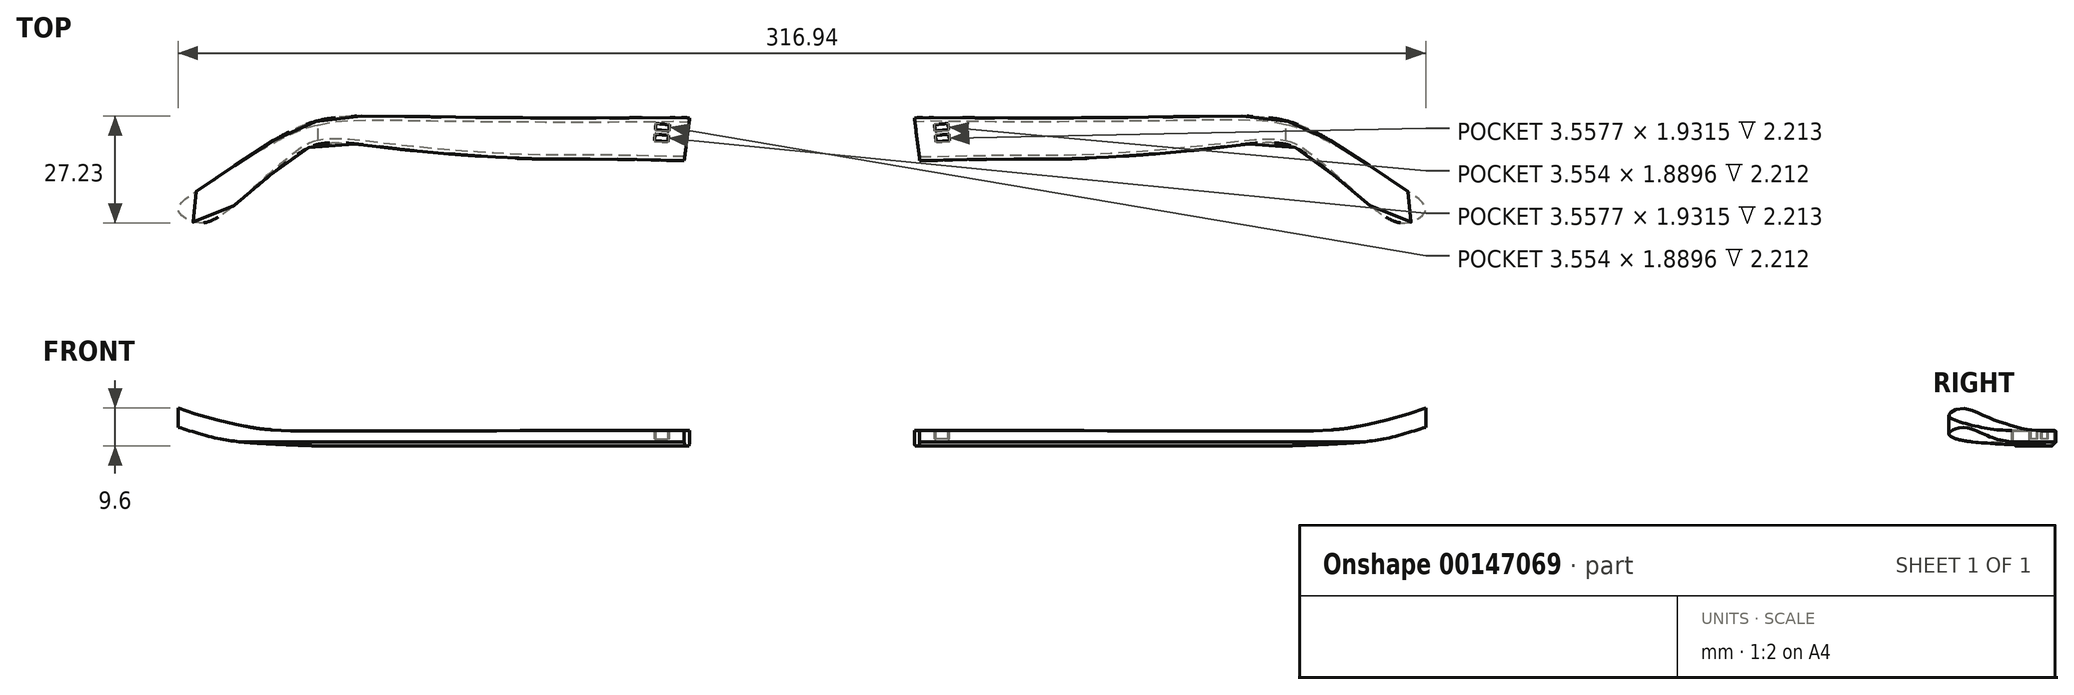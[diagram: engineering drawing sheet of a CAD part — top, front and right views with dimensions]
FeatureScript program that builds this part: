
annotation { "Feature Type Name" : "Feature", "Feature Type Description" : "" }
export const myFeature = defineFeature(function(context is Context, id is Id, definition is map)
    precondition{}
    {
        {
            var Q0;
            Q0=qCreatedBy(makeId("Top.planeOp"),FACE);
            var sketch = newSketch(context, id + "F0", { "sketchPlane" : qUnion([Q0])});
            skFitSpline(sketch, "E0", {"points": [v(-149.74, 2.86) * mm, v(-143.4, 7.26) * mm, v(-129.74, 15.62) * mm, v(-118.6, 18.94) * mm, v(-100.32, 19.28) * mm, v(-73.4, 18.94) * mm, v(-42.28, 18.93) * mm, v(-31.93, 19.03) * mm, v(-29.5, 18.93) * mm, v(-28, 18.65) * mm, v(-25.83, 16.47) * mm, v(-25.2, 12.13) * mm, v(-28.1, 8.49) * mm, v(-29.97, 8.11) * mm, v(-34.44, 8.11) * mm, v(-42.49, 8.3) * mm, v(-61.43, 8.47) * mm, v(-72.57, 8.64) * mm, v(-100.82, 10.8) * mm, v(-115.45, 12.46) * mm, v(-121.1, 12.46) * mm, v(-124.75, 11.63) * mm, v(-129.57, 8.64) * mm, v(-139.71, 0.5) * mm, v(-145.78, -4.53) * mm, v(-151.34, -7.65) * mm, v(-155.73, -7.18) * mm, v(-158.45, -4.45) * mm, v(-156.34, -1.45) * mm, v(-149.74, 2.86) * mm]});
            skSolve(sketch);
        }
        {
            var Q0;
            Q0=makeQuery(id+"F0.imprint","IMPRINT",FACE,{"disambiguationData":[TD([[makeQuery(id+"F0.imprint","IMPRINT",EDGE,{"derivedFrom":sQuery(id+"F0.wireOp",EDGE,"E0")}),-1.0]])]});
            extrude(context, id + "F1", {"entities" : qUnion([Q0]), "depth" : 10 * mm});
        }
        {
            var Q0;
            Q0=qCreatedBy(makeId("Front.planeOp"),FACE);
            var sketch = newSketch(context, id + "F2", { "sketchPlane" : qUnion([Q0])});
            skFitSpline(sketch, "E1", {"points": [v(-27.02, 3.92) * mm, v(-128.04, 3.8) * mm, v(-133.02, 4.02) * mm, v(-138.85, 4.55) * mm, v(-160.68, 10.48) * mm, v(-165.34, 12.18) * mm, v(-167.35, 10.06) * mm, v(-163.96, 6.88) * mm, v(-155.8, 3.92) * mm, v(-147.33, 1.7) * mm, v(-122.96, 0) * mm, v(-19.65, 0) * mm, v(-10.75, 2.75) * mm, v(-13.72, 3.39) * mm, v(-27.02, 3.92) * mm]});
            skSolve(sketch);
        }
        {
            var Q0;
            Q0=makeQuery(id+"F2.imprint","IMPRINT",FACE,{"disambiguationData":[TD([[makeQuery(id+"F2.imprint","IMPRINT",EDGE,{"derivedFrom":sQuery(id+"F2.wireOp",EDGE,"E1")}),1.0]])]});
            extrude(context, id + "F3", {"entities" : qUnion([Q0]), "operationType" : NewBodyOperationType.INTERSECT, "endBound" : BoundingType.SYMMETRIC, "depth" : 60 * mm});
        }
        {
            var Q0;
            Q0=qCreatedBy(makeId("Top.planeOp"),FACE);
            var sketch = newSketch(context, id + "F4", { "sketchPlane" : qUnion([Q0])});
            skLineSegment(sketch, "E2.bottom", {"start": v(-27.52, 26.98) * mm, "end": v(-9.8, 26.98) * mm});
            skLineSegment(sketch, "E2.top", {"start": v(-30.67, 2.24) * mm, "end": v(-9.8, 2.24) * mm});
            skLineSegment(sketch, "E2.left", {"start": v(-27.52, 26.98) * mm, "end": v(-30.67, 2.24) * mm});
            skLineSegment(sketch, "E2.right", {"start": v(-9.8, 26.98) * mm, "end": v(-9.8, 2.24) * mm});
            skSolve(sketch);
        }
        {
            var Q0;
            Q0 = qSketchRegion(id + "F4", true);
            extrude(context, id + "F5", {"entities" : qUnion([Q0]), "operationType" : NewBodyOperationType.REMOVE, "depth" : 25.4 * mm});
        }
        {
            var Q0;
            Q0=qCreatedBy(makeId("Top.planeOp"),FACE);
            var sketch = newSketch(context, id + "F6", { "sketchPlane" : qUnion([Q0])});
            skLineSegment(sketch, "E3.bottom", {"start": v(-40.87, 20.76) * mm, "end": v(-25.79, 20.76) * mm});
            skLineSegment(sketch, "E3.top", {"start": v(-40.87, 5.2) * mm, "end": v(-25.79, 5.2) * mm});
            skLineSegment(sketch, "E3.left", {"start": v(-40.87, 20.76) * mm, "end": v(-40.87, 5.2) * mm});
            skLineSegment(sketch, "E3.right", {"start": v(-25.79, 20.76) * mm, "end": v(-25.79, 5.2) * mm});
            skSolve(sketch);
        }
        {
            var Q0;
            Q0=qCreatedBy(makeId("Top.planeOp"),FACE);
            cPlane(context, id + "F7", {"entities" : qUnion([Q0]), "cplaneType" : CPlaneType.OFFSET, "offset" : 4.5 * mm, "width" : 150 * mm, "height" : 150 * mm});
        }
        {
            var Q0;
            Q0=qCreatedBy(id+"F7.planeOp",FACE);
            var sketch = newSketch(context, id + "F8", { "sketchPlane" : qUnion([Q0])});
            skLineSegment(sketch, "E4.bottom", {"start": v(-37.1, 17.47) * mm, "end": v(-33.68, 17.17) * mm});
            skLineSegment(sketch, "E4.top", {"start": v(-37.47, 13.11) * mm, "end": v(-34.06, 12.82) * mm});
            skLineSegment(sketch, "E4.left", {"start": v(-37.1, 17.47) * mm, "end": v(-37.47, 13.11) * mm});
            skLineSegment(sketch, "E4.right", {"start": v(-33.68, 17.17) * mm, "end": v(-34.06, 12.82) * mm});
            skLineSegment(sketch, "E5.top", {"start": v(-37.33, 14.75) * mm, "end": v(-33.92, 14.45) * mm});
            skLineSegment(sketch, "E6.bottom", {"start": v(-37.29, 15.26) * mm, "end": v(-33.93, 14.97) * mm});
            skLineSegment(sketch, "E6.top", {"start": v(-37.23, 15.88) * mm, "end": v(-33.82, 15.58) * mm});
            skLineSegment(sketch, "E7", {"start": v(-35.07, 18.25) * mm, "end": v(-37.1, 18.25) * mm});
            skSolve(sketch);
        }
        {
            var Q0;
            {var subQ0=sQuery(id+"F8.wireOp",EDGE,"E4.bottom");Q0=makeQuery(id+"F8.imprint","IMPRINT",FACE,{"disambiguationData":[TD([[makeQuery(id+"F8.imprint","IMPRINT",EDGE,{"derivedFrom":subQ0}),-1.0]])]});}
            var Q1;
            {var subQ0=sQuery(id+"F8.wireOp",EDGE,"E4.top");Q1=makeQuery(id+"F8.imprint","IMPRINT",FACE,{"disambiguationData":[TD([[makeQuery(id+"F8.imprint","IMPRINT",EDGE,{"derivedFrom":subQ0}),1.0]])]});}
            extrude(context, id + "F9", {"entities" : qUnion([Q0, Q1]), "operationType" : NewBodyOperationType.REMOVE, "oppositeDirection" : true, "depth" : 2.75 * mm});
        }
        {
            var Q0;
            Q0=makeQuery(id+"F5.boolean.opBoolean","SPLIT",EDGE,{"disambiguationData":[OD(1.0)],"derivedFrom":makeQuery(id+"F1.opExtrude","CAP_EDGE",EDGE,{"disambiguationData":[OSD([sQuery(id+"F0.wireOp",EDGE,"E0")])],"isStart":true})});
            var Q1;
            Q1=makeQuery(id+"F3.boolean.opBoolean","INTERSECT",EDGE,{"disambiguationData":[OD(1.0)],"derivedFrom":[makeQuery(id+"F1.opExtrude","SWEPT_FACE",FACE,{"disambiguationData":[OSD([sQuery(id+"F0.wireOp",EDGE,"E0")])]}),makeQuery(id+"F3.boolean.toolComplement.opBoolean","COPY",FACE,{"derivedFrom":makeQuery(id+"F3.opExtrude","SWEPT_FACE",FACE,{"disambiguationData":[OSD([sQuery(id+"F2.wireOp",EDGE,"E1")])]})})]});
            var Q2;
            Q2=makeQuery(id+"F5.boolean.opBoolean","SPLIT",EDGE,{"disambiguationData":[OD(0.0)],"derivedFrom":makeQuery(id+"F1.opExtrude","CAP_EDGE",EDGE,{"disambiguationData":[OSD([sQuery(id+"F0.wireOp",EDGE,"E0")])],"isStart":true})});
            var Q3;
            Q3=makeQuery(id+"F3.boolean.opBoolean","INTERSECT",EDGE,{"disambiguationData":[OD(0.0)],"derivedFrom":[makeQuery(id+"F1.opExtrude","SWEPT_FACE",FACE,{"disambiguationData":[OSD([sQuery(id+"F0.wireOp",EDGE,"E0")])]}),makeQuery(id+"F3.boolean.toolComplement.opBoolean","COPY",FACE,{"derivedFrom":makeQuery(id+"F3.opExtrude","SWEPT_FACE",FACE,{"disambiguationData":[OSD([sQuery(id+"F2.wireOp",EDGE,"E1")])]})})]});
            chamfer(context, id + "F10", {"entities" : qUnion([Q0, Q1, Q2, Q3]), "width" : 1 * mm, "tangentPropagation" : true});
        }
        {
            var Q0;
            Q0=makeQuery(id+"F1.opExtrude","SWEPT_BODY",BODY,{"disambiguationData":[OSD([sQuery(id+"F0.wireOp",EDGE,"E0")])]});
            var Q1;
            Q1=qCreatedBy(makeId("Right.planeOp"),FACE);
            mirror(context, id + "F11", {"entities" : qUnion([Q0]), "mirrorPlane" : qUnion([Q1])});
        }
    });
